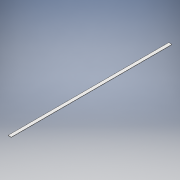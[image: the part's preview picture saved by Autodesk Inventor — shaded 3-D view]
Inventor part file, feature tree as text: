
AUTODESK INVENTOR PART (.ipt)
format: ipt  version: 2018 (Build 220112000, 112)  size: 103,424 bytes
history: native  units: mm
features: sheet_metal_op x1, sketch x1, other x1
ambient origin geometry x8: Origin, YZ Plane, XZ Plane, XY Plane, X Axis, Y Axis, Z Axis, Center Point
bodies: Solid1 (feature_tree)
feature tree (3):
  sheet_metal_op  "Face1"
  sketch  "Sketch1"  dims[d0=24.0mm d1=1208.0mm d2=2.0mm]
  other  "Plate1"
